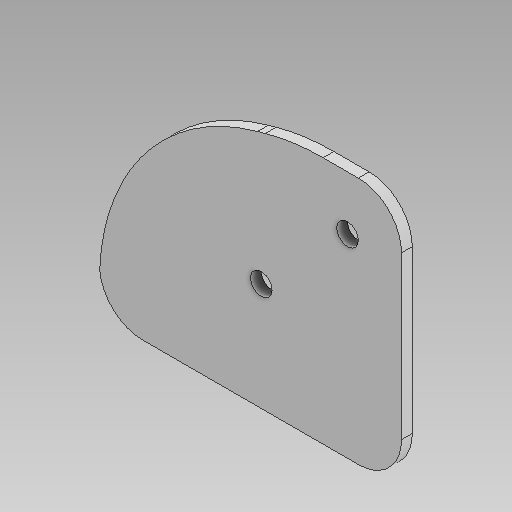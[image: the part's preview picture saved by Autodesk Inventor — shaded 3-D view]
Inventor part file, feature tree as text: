
AUTODESK INVENTOR PART (.ipt)
format: ipt  version: 2025 (Build 290162000, 162)  size: 109,568 bytes
history: native  units: in
note: dims shown in document units (in); Inventor stores cm internally (conversion verified against a paired STEP export)
features: other x1, extrude x1, sketch x1
ambient origin geometry x8: Origin, YZ Plane, XZ Plane, XY Plane, X Axis, Y Axis, Z Axis, Center Point
bodies: Body1 (feature_tree)
feature tree (3):
  other  "솔리드1"
  extrude  "돌출1"  Depth=0.3937in
  sketch  "스케치1"
